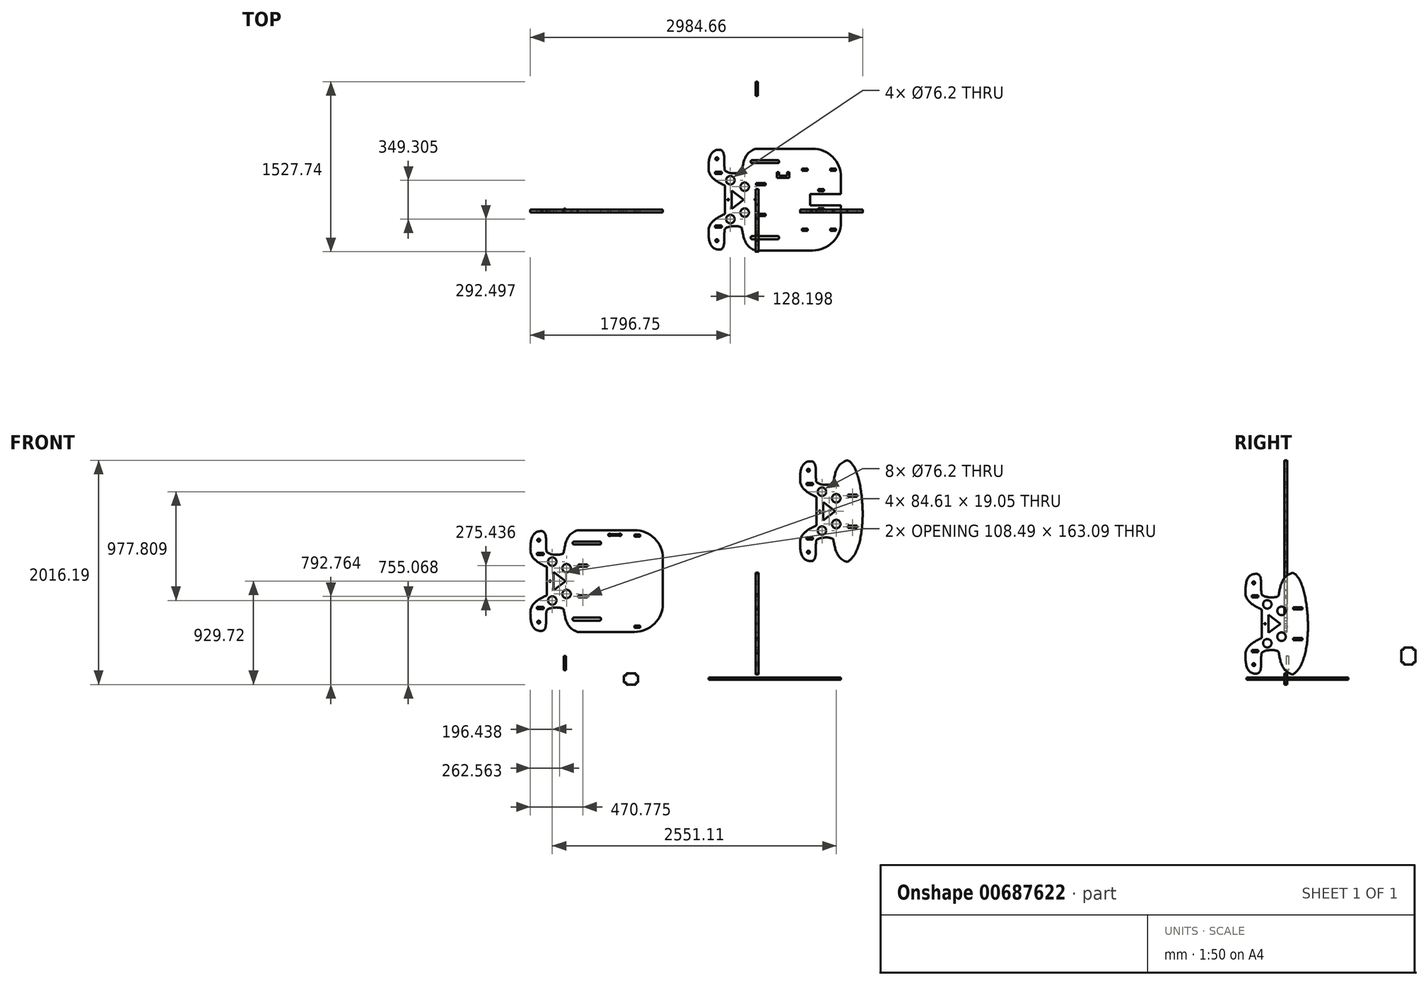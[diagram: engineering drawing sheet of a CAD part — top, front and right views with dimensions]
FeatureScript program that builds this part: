
annotation { "Feature Type Name" : "Feature", "Feature Type Description" : "" }
export const myFeature = defineFeature(function(context is Context, id is Id, definition is map)
    precondition{}
    {
        {
            var Q0;
            Q0=qCreatedBy(makeId("Top.planeOp"),FACE);
            var sketch = newSketch(context, id + "F0", { "sketchPlane" : qUnion([Q0])});
            skLineSegment(sketch, "E0.bottom", {"start": v(0, 548.5) * mm, "end": v(512.74, 548.5) * mm});
            skLineSegment(sketch, "E0.top", {"start": v(0, -365.9) * mm, "end": v(512.74, -365.9) * mm});
            skLineSegment(sketch, "E0.right", {"start": v(766.74, 294.5) * mm, "end": v(766.74, 142.1) * mm});
            skLineSegment(sketch, "E1", {"start": v(-107.03, 91.3) * mm, "end": v(491.23, 91.3) * mm});
            skLineSegment(sketch, "E2", {"start": v(461.94, 548.5) * mm, "end": v(461.94, -365.9) * mm, "construction": true});
            skPoint(sketch, "E3.visualSharp", {"position": v(766.74, -365.9) * mm});
            skArc(sketch, "E3.filletArc", {"start": v(512.74, -365.9) * mm, "mid": v(692.34, -291.51) * mm, "end": v(766.74, -111.9) * mm});
            skPoint(sketch, "E4.visualSharp", {"position": v(766.74, 548.5) * mm});
            skArc(sketch, "E4.filletArc", {"start": v(766.74, 294.5) * mm, "mid": v(692.34, 474.1) * mm, "end": v(512.74, 548.5) * mm});
            skLineSegment(sketch, "E5", {"start": v(210.85, -254.15) * mm, "end": v(210.85, -247.3) * mm});
            skLineSegment(sketch, "E6", {"start": v(200.7, -237.13) * mm, "end": v(-32.99, -237.13) * mm});
            skLineSegment(sketch, "E7", {"start": v(-43.15, -247.3) * mm, "end": v(-43.15, -254.15) * mm});
            skLineSegment(sketch, "E8", {"start": v(-32.99, -264.3) * mm, "end": v(200.7, -264.3) * mm});
            skPoint(sketch, "E9.visualSharp", {"position": v(-43.15, -237.13) * mm});
            skArc(sketch, "E9.filletArc", {"start": v(-32.99, -237.13) * mm, "mid": v(-40.17, -240.1) * mm, "end": v(-43.15, -247.3) * mm});
            skPoint(sketch, "E10.visualSharp", {"position": v(-43.15, -264.3) * mm});
            skArc(sketch, "E10.filletArc", {"start": v(-43.15, -254.15) * mm, "mid": v(-40.17, -261.33) * mm, "end": v(-32.99, -264.3) * mm});
            skPoint(sketch, "E11.visualSharp", {"position": v(210.85, -237.13) * mm});
            skArc(sketch, "E11.filletArc", {"start": v(210.85, -247.3) * mm, "mid": v(207.88, -240.1) * mm, "end": v(200.7, -237.13) * mm});
            skPoint(sketch, "E12.visualSharp", {"position": v(210.85, -264.3) * mm});
            skArc(sketch, "E12.filletArc", {"start": v(200.7, -264.3) * mm, "mid": v(207.88, -261.33) * mm, "end": v(210.85, -254.15) * mm});
            skLineSegment(sketch, "E13.MirrorCS", {"start": v(200.7, 419.71) * mm, "end": v(-32.99, 419.71) * mm});
            skArc(sketch, "E14.MirrorCS", {"start": v(210.85, 429.87) * mm, "mid": v(207.88, 422.69) * mm, "end": v(200.7, 419.71) * mm});
            skArc(sketch, "E15.MirrorCS", {"start": v(-32.99, 419.71) * mm, "mid": v(-40.17, 422.69) * mm, "end": v(-43.15, 429.87) * mm});
            skLineSegment(sketch, "E16.MirrorCS", {"start": v(210.85, 436.73) * mm, "end": v(210.85, 429.87) * mm});
            skLineSegment(sketch, "E17.MirrorCS", {"start": v(-43.15, 429.87) * mm, "end": v(-43.15, 436.73) * mm});
            skLineSegment(sketch, "E18", {"start": v(588.94, -354.2) * mm, "end": v(588.94, 40.5) * mm});
            skLineSegment(sketch, "E19", {"start": v(766.74, 294.5) * mm, "end": v(766.74, 142.1) * mm, "construction": true});
            skFitSpline(sketch, "E20.MirrorCS", {"points": [v(0, -365.9) * mm, v(-122.7, -173.52) * mm, v(-308.54, -21.5) * mm], "startDerivative": vector(-596.34, 198.24) * mm, "endDerivative": vector(-875.38, 6.78) * mm});
            skPoint(sketch, "E21", {"position": v(-43.15, -250.72) * mm});
            skLineSegment(sketch, "E22.MirrorCS", {"start": v(124.5, 91.3) * mm, "end": v(124.5, 90.53) * mm});
            skPoint(sketch, "E23.orphan", {"position": v(-15.2, 268.33) * mm});
            skLineSegment(sketch, "E24", {"start": v(-214.5, 172.07) * mm, "end": v(-214.5, 8.99) * mm});
            skCircle(sketch, "E25", {"center": v(-245.87, 90.53) * mm, "radius": 6.35 * mm});
            skCircle(sketch, "E26", {"center": v(-98.19, -25.5) * mm, "radius": 38.1 * mm});
            skPoint(sketch, "E27.positionSnap0", {"position": v(-320.15, -344.34) * mm});
            skPoint(sketch, "E28.MirrorP", {"position": v(-43.15, 431.78) * mm});
            skPoint(sketch, "E29.MirrorP", {"position": v(-43.15, 445.37) * mm});
            skPoint(sketch, "E30.MirrorP", {"position": v(-43.15, 418.19) * mm});
            skLineSegment(sketch, "E31", {"start": v(-214.5, 8.99) * mm, "end": v(-106.02, 90.53) * mm});
            skLineSegment(sketch, "E32.MirrorCS", {"start": v(-214.5, 172.07) * mm, "end": v(-106.02, 90.53) * mm});
            skCircle(sketch, "E33.MirrorC", {"center": v(-226.39, -84.12) * mm, "radius": 38.1 * mm});
            skCircle(sketch, "E34.MirrorC", {"center": v(-347.9, -277.34) * mm, "radius": 12.7 * mm});
            skPoint(sketch, "E35.MirrorP", {"position": v(-324.04, -277.34) * mm});
            skFitSpline(sketch, "E36.MirrorCS", {"points": [v(-320.15, -358.3) * mm, v(-277.34, -173.78) * mm], "startDerivative": vector(168, 45.32) * mm, "endDerivative": vector(42.54, 297.2) * mm});
            skFitSpline(sketch, "E37.MirrorCS", {"points": [v(-320.15, -358.3) * mm, v(-407.1, -21.15) * mm], "startDerivative": vector(-410.48, -21.33) * mm, "endDerivative": vector(48.12, 416.26) * mm});
            skFitSpline(sketch, "E38", {"points": [v(-123.95, -167.42) * mm, v(-277.34, -173.78) * mm], "startDerivative": vector(-0.87, 82.52) * mm, "endDerivative": vector(-81, -110.74) * mm});
            skFitSpline(sketch, "E39", {"points": [v(-276.57, -37.66) * mm, v(-422.21, -174.57) * mm], "startDerivative": vector(-229.66, -105.01) * mm, "endDerivative": vector(-27.76, -191.38) * mm});
            skFitSpline(sketch, "E40.MirrorCS", {"points": [v(0, 548.5) * mm, v(-122.7, 356.1) * mm, v(-308.54, 204.08) * mm], "startDerivative": vector(-596.34, -198.24) * mm, "endDerivative": vector(-875.38, -6.78) * mm});
            skLineSegment(sketch, "E41.MirrorCS", {"start": v(-43.15, 428.35) * mm, "end": v(-43.15, 435.2) * mm});
            skArc(sketch, "E42.MirrorCS", {"start": v(200.7, 445.37) * mm, "mid": v(207.88, 442.4) * mm, "end": v(210.85, 435.2) * mm});
            skLineSegment(sketch, "E43.MirrorCS", {"start": v(210.85, 435.2) * mm, "end": v(210.85, 428.35) * mm});
            skArc(sketch, "E44.MirrorCS", {"start": v(-43.15, 435.2) * mm, "mid": v(-40.17, 442.4) * mm, "end": v(-32.99, 445.37) * mm});
            skCircle(sketch, "E45.MirrorC", {"center": v(-347.9, 458.4) * mm, "radius": 12.7 * mm});
            skFitSpline(sketch, "E46.MirrorCS", {"points": [v(-320.15, 539.35) * mm, v(-407.1, 202.21) * mm], "startDerivative": vector(-410.48, 21.33) * mm, "endDerivative": vector(48.12, -416.26) * mm});
            skFitSpline(sketch, "E47.MirrorCS", {"points": [v(-276.57, 218.72) * mm, v(-422.21, 355.63) * mm], "startDerivative": vector(-229.66, 105.01) * mm, "endDerivative": vector(-27.76, 191.38) * mm});
            skCircle(sketch, "E48.MirrorC", {"center": v(-98.19, 206.56) * mm, "radius": 38.1 * mm});
            skPoint(sketch, "E49.MirrorP", {"position": v(-324.04, 458.4) * mm});
            skFitSpline(sketch, "E50.MirrorCS", {"points": [v(-123.95, 348.48) * mm, v(-277.34, 354.84) * mm], "startDerivative": vector(-0.87, -82.52) * mm, "endDerivative": vector(-81, 110.74) * mm});
            skLineSegment(sketch, "E51.MirrorCS", {"start": v(-32.99, 445.37) * mm, "end": v(200.7, 445.37) * mm});
            skCircle(sketch, "E52.MirrorC", {"center": v(-226.39, 265.18) * mm, "radius": 38.1 * mm});
            skPoint(sketch, "E53.MirrorP", {"position": v(210.85, 418.19) * mm});
            skPoint(sketch, "E54.MirrorP", {"position": v(-320.15, 525.4) * mm});
            skFitSpline(sketch, "E55.MirrorCS", {"points": [v(-320.15, 539.35) * mm, v(-277.34, 354.84) * mm], "startDerivative": vector(168, -45.32) * mm, "endDerivative": vector(42.54, -297.2) * mm});
            skPoint(sketch, "E56.MirrorP", {"position": v(210.85, 445.37) * mm});
            skPoint(sketch, "E57.MirrorP", {"position": v(0, 546.97) * mm});
            skLineSegment(sketch, "E58", {"start": v(-276.57, -37.66) * mm, "end": v(-276.57, 218.72) * mm});
            skFitSpline(sketch, "E59", {"points": [v(-123.95, 348.48) * mm, v(-123.95, 350) * mm], "startDerivative": vector(0.09, 0.95) * mm, "endDerivative": vector(0.33, 1.62) * mm});
            skLineSegment(sketch, "E60.MirrorCS", {"start": v(5.64, 219.48) * mm, "end": v(90.26, 219.48) * mm});
            skLineSegment(sketch, "E61.MirrorCS", {"start": v(5.64, 238.53) * mm, "end": v(5.64, 219.48) * mm});
            skLineSegment(sketch, "E62.MirrorCS", {"start": v(90.26, 238.53) * mm, "end": v(90.26, 219.48) * mm});
            skLineSegment(sketch, "E63.MirrorCS", {"start": v(5.64, 238.53) * mm, "end": v(90.26, 238.53) * mm});
            skLineSegment(sketch, "E64.MirrorCS", {"start": v(5.64, -36.9) * mm, "end": v(90.26, -36.9) * mm});
            skLineSegment(sketch, "E65.MirrorCS", {"start": v(5.64, -55.95) * mm, "end": v(90.26, -55.95) * mm});
            skLineSegment(sketch, "E66.MirrorCS", {"start": v(5.64, -55.95) * mm, "end": v(5.64, -36.9) * mm});
            skLineSegment(sketch, "E67.MirrorCS", {"start": v(90.26, -55.95) * mm, "end": v(90.26, -36.9) * mm});
            skLineSegment(sketch, "E68.bottom", {"start": v(-362.9, 342.54) * mm, "end": v(-305.3, 342.54) * mm});
            skLineSegment(sketch, "E68.top", {"start": v(-362.9, 323.49) * mm, "end": v(-305.3, 323.49) * mm});
            skLineSegment(sketch, "E68.left", {"start": v(-362.9, 342.54) * mm, "end": v(-362.9, 323.49) * mm});
            skLineSegment(sketch, "E68.right", {"start": v(-305.3, 342.54) * mm, "end": v(-305.3, 323.49) * mm});
            skLineSegment(sketch, "E69", {"start": v(-106.02, 90.53) * mm, "end": v(-545.67, 90.53) * mm});
            skLineSegment(sketch, "E70.MirrorCS", {"start": v(-362.9, -161.48) * mm, "end": v(-305.3, -161.48) * mm});
            skLineSegment(sketch, "E71.MirrorCS", {"start": v(-362.9, -142.43) * mm, "end": v(-305.3, -142.43) * mm});
            skLineSegment(sketch, "E72.MirrorCS", {"start": v(-362.9, -161.48) * mm, "end": v(-362.9, -142.43) * mm});
            skLineSegment(sketch, "E73.MirrorCS", {"start": v(-305.3, -161.48) * mm, "end": v(-305.3, -142.43) * mm});
            skLineSegment(sketch, "E74", {"start": v(-422.21, 355.63) * mm, "end": v(-277.34, 354.84) * mm, "construction": true});
            skPoint(sketch, "E75.endSnap0", {"position": v(210.85, 433.3) * mm});
            skPoint(sketch, "E76", {"position": v(461.94, 370.7) * mm});
            skPoint(sketch, "E77", {"position": v(461.94, -188.1) * mm});
            skLineSegment(sketch, "E78", {"start": v(755.04, 370.7) * mm, "end": v(223.96, 370.7) * mm, "construction": true});
            skLineSegment(sketch, "E79.bottom", {"start": v(418.05, 370.7) * mm, "end": v(468.85, 370.7) * mm});
            skLineSegment(sketch, "E79.top", {"start": v(418.05, 351.64) * mm, "end": v(468.85, 351.64) * mm});
            skLineSegment(sketch, "E79.left", {"start": v(418.05, 370.7) * mm, "end": v(418.05, 351.64) * mm});
            skLineSegment(sketch, "E79.right", {"start": v(468.85, 370.7) * mm, "end": v(468.85, 351.64) * mm});
            skLineSegment(sketch, "E80.bottom", {"start": v(672.05, 370.7) * mm, "end": v(722.85, 370.7) * mm});
            skLineSegment(sketch, "E80.top", {"start": v(672.05, 351.64) * mm, "end": v(722.85, 351.64) * mm});
            skLineSegment(sketch, "E80.left", {"start": v(672.05, 370.7) * mm, "end": v(672.05, 351.64) * mm});
            skLineSegment(sketch, "E80.right", {"start": v(722.85, 370.7) * mm, "end": v(722.85, 351.64) * mm});
            skLineSegment(sketch, "E81.MirrorCS", {"start": v(418.05, -188.1) * mm, "end": v(468.85, -188.1) * mm});
            skLineSegment(sketch, "E82.MirrorCS", {"start": v(418.05, -188.1) * mm, "end": v(418.05, -169.06) * mm});
            skLineSegment(sketch, "E83.MirrorCS", {"start": v(418.05, -169.06) * mm, "end": v(468.85, -169.06) * mm});
            skLineSegment(sketch, "E84.MirrorCS", {"start": v(468.85, -188.1) * mm, "end": v(468.85, -169.06) * mm});
            skLineSegment(sketch, "E85.MirrorCS", {"start": v(672.05, -188.1) * mm, "end": v(722.85, -188.1) * mm});
            skLineSegment(sketch, "E86.MirrorCS", {"start": v(672.05, -188.1) * mm, "end": v(672.05, -169.06) * mm});
            skLineSegment(sketch, "E87.MirrorCS", {"start": v(672.05, -169.06) * mm, "end": v(722.85, -169.06) * mm});
            skLineSegment(sketch, "E88.MirrorCS", {"start": v(722.85, -188.1) * mm, "end": v(722.85, -169.06) * mm});
            skPoint(sketch, "E89", {"position": v(461.94, 91.3) * mm});
            skPoint(sketch, "E90", {"position": v(461.94, 40.5) * mm});
            skPoint(sketch, "E91", {"position": v(461.94, 142.1) * mm});
            skLineSegment(sketch, "E92.left", {"start": v(491.23, 40.5) * mm, "end": v(491.23, 142.1) * mm});
            skLineSegment(sketch, "E93.bottom", {"start": v(563.54, 167.5) * mm, "end": v(614.34, 167.5) * mm});
            skLineSegment(sketch, "E93.top", {"start": v(563.54, 186.54) * mm, "end": v(614.34, 186.54) * mm});
            skLineSegment(sketch, "E93.left", {"start": v(563.54, 167.5) * mm, "end": v(563.54, 186.54) * mm});
            skLineSegment(sketch, "E93.right", {"start": v(614.34, 167.5) * mm, "end": v(614.34, 186.54) * mm});
            skLineSegment(sketch, "E94.MirrorCS", {"start": v(563.54, 15.1) * mm, "end": v(614.34, 15.1) * mm});
            skLineSegment(sketch, "E95.MirrorCS", {"start": v(563.54, -3.96) * mm, "end": v(614.34, -3.96) * mm});
            skLineSegment(sketch, "E96.MirrorCS", {"start": v(563.54, 15.1) * mm, "end": v(563.54, -3.96) * mm});
            skLineSegment(sketch, "E97.MirrorCS", {"start": v(614.34, 15.1) * mm, "end": v(614.34, -3.96) * mm});
            skCircle(sketch, "E98", {"center": v(0, 91.3) * mm, "radius": 8.9 * mm});
            skPoint(sketch, "E98.centerSnap0", {"position": v(697.45, -169.06) * mm});
            skLineSegment(sketch, "E99", {"start": v(491.23, 142.1) * mm, "end": v(766.74, 142.1) * mm});
            skLineSegment(sketch, "E100", {"start": v(491.23, 40.5) * mm, "end": v(766.74, 40.5) * mm});
            skLineSegment(sketch, "E101.trimOffspring", {"start": v(766.74, 40.5) * mm, "end": v(766.74, -111.9) * mm, "construction": true});
            skLineSegment(sketch, "E102.trimOffspring", {"start": v(766.74, 40.5) * mm, "end": v(766.74, -111.9) * mm});
            skPoint(sketch, "E103.orphan", {"position": v(766.74, 91.3) * mm});
            skLineSegment(sketch, "E104.trimOffspring", {"start": v(588.94, 142.1) * mm, "end": v(588.94, 536.8) * mm});
            skLineSegment(sketch, "E105", {"start": v(246.34, 305.67) * mm, "end": v(281.83, 305.67) * mm});
            skLineSegment(sketch, "E106", {"start": v(281.83, 305.67) * mm, "end": v(281.83, 337.71) * mm});
            skLineSegment(sketch, "E107", {"start": v(281.83, 337.71) * mm, "end": v(300.88, 337.71) * mm});
            skLineSegment(sketch, "E108", {"start": v(300.88, 337.71) * mm, "end": v(300.88, 286.62) * mm});
            skLineSegment(sketch, "E109", {"start": v(300.88, 286.62) * mm, "end": v(246.34, 286.62) * mm});
            skPoint(sketch, "E110.startSnap0", {"position": v(246.34, 305.67) * mm});
            skPoint(sketch, "E111.end.orphan", {"position": v(210.85, 338.7) * mm});
            skPoint(sketch, "E112.orphan", {"position": v(210.85, 305.67) * mm});
            skLineSegment(sketch, "E113.MirrorCS", {"start": v(191.8, 337.71) * mm, "end": v(191.8, 286.62) * mm});
            skLineSegment(sketch, "E114.MirrorCS", {"start": v(210.85, 337.71) * mm, "end": v(191.8, 337.71) * mm});
            skLineSegment(sketch, "E115.MirrorCS", {"start": v(210.85, 305.67) * mm, "end": v(210.85, 337.71) * mm});
            skLineSegment(sketch, "E116.MirrorCS", {"start": v(246.34, 305.67) * mm, "end": v(210.85, 305.67) * mm});
            skLineSegment(sketch, "E117.MirrorCS", {"start": v(191.8, 286.62) * mm, "end": v(246.34, 286.62) * mm});
            skPoint(sketch, "E118.orphan", {"position": v(246.34, 360) * mm});
            skSolve(sketch);
        }
        {
            var Q0;
            Q0=qCreatedBy(makeId("Front.planeOp"),FACE);
            var sketch = newSketch(context, id + "F1", { "sketchPlane" : qUnion([Q0])});
            skLineSegment(sketch, "E119.bottom", {"start": v(-1714.56, 86.36) * mm, "end": v(-1724.72, 86.36) * mm});
            skLineSegment(sketch, "E119.top", {"start": v(-1714.56, 213.36) * mm, "end": v(-1724.72, 213.36) * mm});
            skLineSegment(sketch, "E119.left", {"start": v(-1714.56, 86.36) * mm, "end": v(-1714.56, 213.36) * mm});
            skLineSegment(sketch, "E119.right", {"start": v(-1724.72, 86.36) * mm, "end": v(-1724.72, 213.36) * mm});
            skPoint(sketch, "E119.middle", {"position": v(-1719.64, 149.86) * mm});
            skSolve(sketch);
        }
        {
            var Q0;
            Q0=makeQuery(id+"F1.imprint","IMPRINT",FACE,{"disambiguationData":[TD([[makeQuery(id+"F1.imprint","IMPRINT",EDGE,{"derivedFrom":sQuery(id+"F1.wireOp",EDGE,"E119.bottom")}),-1.0]])]});
            var Q1;
            Q1=sQuery(id+"F1.wireOp",EDGE,"E119.left");
            revolve(context, id + "F2", {"entities" : qUnion([Q0]), "axis" : qUnion([Q1]), "revolveType" : RevolveType.FULL});
        }
        {
            var Q0;
            Q0=qSketchRegion(id+"F0",true);
            extrude(context, id + "F3", {"entities" : qUnion([Q0]), "depth" : 19.05 * mm, "offsetDistance" : 25.4 * mm});
        }
        {
            var Q0;
            Q0=qCreatedBy(makeId("Right.planeOp"),FACE);
            var sketch = newSketch(context, id + "F4", { "sketchPlane" : qUnion([Q0])});
            skFitSpline(sketch, "E120.MirrorCS", {"points": [v(46.21, 47.06) * mm, v(-76.5, 239.45) * mm, v(-262.33, 391.47) * mm], "startDerivative": vector(-596.34, 198.24) * mm, "endDerivative": vector(-875.38, 6.78) * mm});
            skLineSegment(sketch, "E121", {"start": v(-168.3, 585.05) * mm, "end": v(-168.3, 421.96) * mm});
            skCircle(sketch, "E122", {"center": v(-199.66, 503.5) * mm, "radius": 6.35 * mm});
            skCircle(sketch, "E123", {"center": v(-51.98, 387.47) * mm, "radius": 38.1 * mm});
            skPoint(sketch, "E124.positionSnap0", {"position": v(-273.94, 68.63) * mm});
            skLineSegment(sketch, "E125", {"start": v(-168.3, 421.96) * mm, "end": v(-59.8, 503.5) * mm});
            skLineSegment(sketch, "E126.MirrorCS", {"start": v(-168.3, 585.05) * mm, "end": v(-59.8, 503.5) * mm});
            skCircle(sketch, "E127.MirrorC", {"center": v(-180.17, 328.85) * mm, "radius": 38.1 * mm});
            skCircle(sketch, "E128.MirrorC", {"center": v(-301.7, 135.64) * mm, "radius": 12.7 * mm});
            skPoint(sketch, "E129.MirrorP", {"position": v(-277.83, 135.64) * mm});
            skFitSpline(sketch, "E130.MirrorCS", {"points": [v(-273.94, 54.68) * mm, v(-231.14, 240.68) * mm], "startDerivative": vector(168, 45.32) * mm, "endDerivative": vector(42.54, 297.2) * mm});
            skFitSpline(sketch, "E131.MirrorCS", {"points": [v(-273.94, 54.68) * mm, v(-360.89, 391.82) * mm], "startDerivative": vector(-410.48, -21.33) * mm, "endDerivative": vector(48.12, 416.26) * mm});
            skFitSpline(sketch, "E132", {"points": [v(-77.74, 245.55) * mm, v(-231.14, 240.68) * mm], "startDerivative": vector(-0.87, 82.52) * mm, "endDerivative": vector(-81, -110.74) * mm});
            skFitSpline(sketch, "E133", {"points": [v(-230.36, 375.3) * mm, v(-376, 238.4) * mm], "startDerivative": vector(-229.66, -105.01) * mm, "endDerivative": vector(-27.76, -191.38) * mm});
            skFitSpline(sketch, "E134.MirrorCS", {"points": [v(46.21, 961.46) * mm, v(-76.5, 769.07) * mm, v(-262.33, 617.06) * mm], "startDerivative": vector(-596.34, -198.24) * mm, "endDerivative": vector(-875.38, -6.78) * mm});
            skCircle(sketch, "E135.MirrorC", {"center": v(-301.7, 871.37) * mm, "radius": 12.7 * mm});
            skFitSpline(sketch, "E136.MirrorCS", {"points": [v(-273.94, 952.33) * mm, v(-360.89, 615.19) * mm], "startDerivative": vector(-410.48, 21.33) * mm, "endDerivative": vector(48.12, -416.26) * mm});
            skFitSpline(sketch, "E137.MirrorCS", {"points": [v(-230.36, 631.7) * mm, v(-376, 768.6) * mm], "startDerivative": vector(-229.66, 105.01) * mm, "endDerivative": vector(-27.76, 191.38) * mm});
            skCircle(sketch, "E138.MirrorC", {"center": v(-51.98, 619.54) * mm, "radius": 38.1 * mm});
            skPoint(sketch, "E139.MirrorP", {"position": v(-277.83, 871.37) * mm});
            skFitSpline(sketch, "E140.MirrorCS", {"points": [v(-77.74, 761.46) * mm, v(-231.13, 767.8) * mm], "startDerivative": vector(-0.87, -82.52) * mm, "endDerivative": vector(-81, 110.74) * mm});
            skCircle(sketch, "E141.MirrorC", {"center": v(-180.17, 678.15) * mm, "radius": 38.1 * mm});
            skPoint(sketch, "E142.MirrorP", {"position": v(-273.94, 938.38) * mm});
            skFitSpline(sketch, "E143.MirrorCS", {"points": [v(-273.94, 952.33) * mm, v(-231.13, 767.8) * mm], "startDerivative": vector(168, -45.32) * mm, "endDerivative": vector(42.54, -297.2) * mm});
            skLineSegment(sketch, "E144", {"start": v(-230.36, 375.3) * mm, "end": v(-230.36, 631.7) * mm});
            skFitSpline(sketch, "E145", {"points": [v(-77.74, 761.46) * mm, v(-77.74, 762.98) * mm], "startDerivative": vector(0.09, 0.95) * mm, "endDerivative": vector(0.33, 1.62) * mm});
            skFitSpline(sketch, "E146", {"points": [v(46.21, 961.46) * mm, v(46.21, 47.06) * mm], "startDerivative": vector(461.05, -112.6) * mm, "endDerivative": vector(-642.98, -332.06) * mm});
            skLineSegment(sketch, "E147.bottom", {"start": v(51.86, 632.46) * mm, "end": v(136.47, 632.46) * mm});
            skLineSegment(sketch, "E147.top", {"start": v(51.86, 651.5) * mm, "end": v(136.47, 651.5) * mm});
            skLineSegment(sketch, "E147.left", {"start": v(51.86, 632.46) * mm, "end": v(51.86, 651.5) * mm});
            skLineSegment(sketch, "E147.right", {"start": v(136.47, 632.46) * mm, "end": v(136.47, 651.5) * mm});
            skLineSegment(sketch, "E148", {"start": v(-59.8, 503.5) * mm, "end": v(281.17, 503.5) * mm});
            skLineSegment(sketch, "E149", {"start": v(141.4, 175.84) * mm, "end": v(13.23, 175.84) * mm});
            skLineSegment(sketch, "E150", {"start": v(3.07, 165.68) * mm, "end": v(3.07, 158.82) * mm});
            skLineSegment(sketch, "E151", {"start": v(13.23, 148.66) * mm, "end": v(130.44, 148.66) * mm});
            skPoint(sketch, "E152.visualSharp", {"position": v(3.07, 175.84) * mm});
            skArc(sketch, "E152.filletArc", {"start": v(13.23, 175.84) * mm, "mid": v(6.04, 172.87) * mm, "end": v(3.07, 165.68) * mm});
            skPoint(sketch, "E153.visualSharp", {"position": v(3.07, 148.66) * mm});
            skArc(sketch, "E153.filletArc", {"start": v(3.07, 158.82) * mm, "mid": v(6.04, 151.64) * mm, "end": v(13.23, 148.66) * mm});
            skFitSpline(sketch, "E154.MirrorCS", {"points": [v(46.21, 47.06) * mm, v(-76.5, 239.45) * mm, v(-262.33, 391.47) * mm], "startDerivative": vector(-596.34, 198.24) * mm, "endDerivative": vector(-875.38, 6.78) * mm});
            skPoint(sketch, "E155", {"position": v(3.07, 162.25) * mm});
            skArc(sketch, "E156.MirrorCS", {"start": v(13.23, 831.16) * mm, "mid": v(6.04, 834.14) * mm, "end": v(3.07, 841.32) * mm});
            skArc(sketch, "E157.MirrorCS", {"start": v(3.07, 848.18) * mm, "mid": v(6.04, 855.36) * mm, "end": v(13.23, 858.34) * mm});
            skLineSegment(sketch, "E158.MirrorCS", {"start": v(3.07, 841.32) * mm, "end": v(3.07, 848.18) * mm});
            skLineSegment(sketch, "E159.MirrorCS", {"start": v(137.14, 831.16) * mm, "end": v(13.23, 831.16) * mm});
            skPoint(sketch, "E160.MirrorP", {"position": v(3.07, 858.34) * mm});
            skPoint(sketch, "E161.MirrorP", {"position": v(3.07, 831.16) * mm});
            skPoint(sketch, "E162.MirrorP", {"position": v(3.07, 844.75) * mm});
            skLineSegment(sketch, "E163.MirrorCS", {"start": v(13.23, 858.34) * mm, "end": v(127.47, 858.34) * mm});
            skLineSegment(sketch, "E164.MirrorCS", {"start": v(51.86, 355.5) * mm, "end": v(136.47, 355.5) * mm});
            skLineSegment(sketch, "E165.MirrorCS", {"start": v(51.86, 374.55) * mm, "end": v(136.47, 374.55) * mm});
            skLineSegment(sketch, "E166.MirrorCS", {"start": v(51.86, 374.55) * mm, "end": v(51.86, 355.5) * mm});
            skLineSegment(sketch, "E167.MirrorCS", {"start": v(136.47, 374.55) * mm, "end": v(136.47, 355.5) * mm});
            skLineSegment(sketch, "E168", {"start": v(-231.14, 240.68) * mm, "end": v(-376, 238.4) * mm, "construction": true});
            skLineSegment(sketch, "E169.bottom", {"start": v(-260.66, 267.57) * mm, "end": v(-318.26, 267.57) * mm});
            skLineSegment(sketch, "E169.top", {"start": v(-260.66, 248.52) * mm, "end": v(-318.26, 248.52) * mm});
            skLineSegment(sketch, "E169.left", {"start": v(-260.66, 267.57) * mm, "end": v(-260.66, 248.52) * mm});
            skLineSegment(sketch, "E169.right", {"start": v(-318.26, 267.57) * mm, "end": v(-318.26, 248.52) * mm});
            skLineSegment(sketch, "E170.MirrorCS", {"start": v(-260.66, 739.44) * mm, "end": v(-318.26, 739.44) * mm});
            skLineSegment(sketch, "E171.MirrorCS", {"start": v(-260.66, 758.49) * mm, "end": v(-318.26, 758.49) * mm});
            skLineSegment(sketch, "E172.MirrorCS", {"start": v(-318.26, 739.44) * mm, "end": v(-318.26, 758.49) * mm});
            skLineSegment(sketch, "E173.MirrorCS", {"start": v(-260.66, 739.44) * mm, "end": v(-260.66, 758.49) * mm});
            skSolve(sketch);
        }
        {
            var Q0;
            Q0=qSketchRegion(id+"F4",true);
            extrude(context, id + "F5", {"entities" : qUnion([Q0]), "depth" : 25.4 * mm, "offsetDistance" : 25.4 * mm});
        }
        {
            var Q0;
            Q0=qCreatedBy(makeId("Right.planeOp"),FACE);
            var sketch = newSketch(context, id + "F6", { "sketchPlane" : qUnion([Q0])});
            skLineSegment(sketch, "E174.bottom", {"start": v(1024.12, 270.76) * mm, "end": v(1151.12, 270.76) * mm});
            skLineSegment(sketch, "E174.top", {"start": v(1024.12, 156.46) * mm, "end": v(1151.12, 156.46) * mm});
            skLineSegment(sketch, "E174.left", {"start": v(1024.12, 270.76) * mm, "end": v(1024.12, 156.46) * mm});
            skLineSegment(sketch, "E174.right", {"start": v(1151.12, 270.76) * mm, "end": v(1151.12, 156.46) * mm});
            skLineSegment(sketch, "E175", {"start": v(1087.62, 270.76) * mm, "end": v(1087.62, 156.46) * mm, "construction": true});
            skLineSegment(sketch, "E176", {"start": v(1045.31, 270.76) * mm, "end": v(1045.31, 289.8) * mm});
            skLineSegment(sketch, "E177", {"start": v(1045.31, 289.8) * mm, "end": v(1129.93, 289.8) * mm});
            skLineSegment(sketch, "E178", {"start": v(1129.93, 289.8) * mm, "end": v(1129.93, 270.76) * mm});
            skLineSegment(sketch, "E179", {"start": v(1024.12, 213.6) * mm, "end": v(1151.12, 213.6) * mm, "construction": true});
            skLineSegment(sketch, "E180.MirrorCS", {"start": v(1045.31, 156.46) * mm, "end": v(1045.31, 137.4) * mm});
            skLineSegment(sketch, "E181.MirrorCS", {"start": v(1045.31, 137.4) * mm, "end": v(1129.93, 137.4) * mm});
            skLineSegment(sketch, "E182.MirrorCS", {"start": v(1129.93, 137.4) * mm, "end": v(1129.93, 156.46) * mm});
            skSolve(sketch);
        }
        {
            var Q0;
            {var subQ0=sQuery(id+"F6.wireOp",EDGE,"E174.left");Q0=makeQuery(id+"F6.imprint","IMPRINT",FACE,{"disambiguationData":[TD([[makeQuery(id+"F6.imprint","IMPRINT",EDGE,{"derivedFrom":subQ0}),1.0]])]});}
            var Q1;
            {var subQ0=sQuery(id+"F6.wireOp",EDGE,"E176");Q1=makeQuery(id+"F6.imprint","IMPRINT",FACE,{"disambiguationData":[TD([[makeQuery(id+"F6.imprint","IMPRINT",EDGE,{"derivedFrom":subQ0}),-1.0]])]});}
            var Q2;
            {var subQ0=sQuery(id+"F6.wireOp",EDGE,"E180.MirrorCS");Q2=makeQuery(id+"F6.imprint","IMPRINT",FACE,{"disambiguationData":[TD([[makeQuery(id+"F6.imprint","IMPRINT",EDGE,{"derivedFrom":subQ0}),1.0]])]});}
            extrude(context, id + "F7", {"entities" : qUnion([Q0, Q1, Q2]), "depth" : 19.05 * mm, "offsetDistance" : 25.4 * mm});
        }
        {
            var Q0;
            Q0=qCreatedBy(makeId("Front.planeOp"),FACE);
            var sketch = newSketch(context, id + "F8", { "sketchPlane" : qUnion([Q0])});
            skLineSegment(sketch, "E183.bottom", {"start": v(-1182.42, 39.8) * mm, "end": v(-1055.42, 39.8) * mm});
            skLineSegment(sketch, "E183.top", {"start": v(-1182.42, -23.7) * mm, "end": v(-1055.42, -23.7) * mm});
            skLineSegment(sketch, "E183.left", {"start": v(-1182.42, 39.8) * mm, "end": v(-1182.42, -23.7) * mm});
            skLineSegment(sketch, "E183.right", {"start": v(-1055.42, 39.8) * mm, "end": v(-1055.42, -23.7) * mm});
            skLineSegment(sketch, "E184", {"start": v(-1118.92, 39.8) * mm, "end": v(-1118.92, -23.7) * mm, "construction": true});
            skLineSegment(sketch, "E185", {"start": v(-1161.23, 39.8) * mm, "end": v(-1161.23, 58.85) * mm});
            skLineSegment(sketch, "E186", {"start": v(-1161.23, 58.85) * mm, "end": v(-1076.62, 58.85) * mm});
            skLineSegment(sketch, "E187", {"start": v(-1076.62, 58.85) * mm, "end": v(-1076.62, 39.8) * mm});
            skLineSegment(sketch, "E188", {"start": v(-1182.42, 8.05) * mm, "end": v(-1055.42, 8.05) * mm, "construction": true});
            skLineSegment(sketch, "E189.MirrorCS", {"start": v(-1161.23, -23.7) * mm, "end": v(-1161.23, -42.75) * mm});
            skLineSegment(sketch, "E190.MirrorCS", {"start": v(-1161.23, -42.75) * mm, "end": v(-1076.62, -42.75) * mm});
            skLineSegment(sketch, "E191.MirrorCS", {"start": v(-1076.62, -42.75) * mm, "end": v(-1076.62, -23.7) * mm});
            skLineSegment(sketch, "E192.bottom", {"start": v(-1600.32, 1344.93) * mm, "end": v(-1087.58, 1344.93) * mm});
            skLineSegment(sketch, "E192.top", {"start": v(-1600.32, 430.53) * mm, "end": v(-1087.58, 430.53) * mm});
            skLineSegment(sketch, "E192.right", {"start": v(-833.58, 1090.93) * mm, "end": v(-833.58, 684.53) * mm});
            skLineSegment(sketch, "E193", {"start": v(-1707.35, 887.73) * mm, "end": v(-833.58, 887.73) * mm});
            skLineSegment(sketch, "E194", {"start": v(-1138.38, 1344.93) * mm, "end": v(-1138.38, 430.53) * mm, "construction": true});
            skPoint(sketch, "E195.visualSharp", {"position": v(-833.58, 430.53) * mm});
            skArc(sketch, "E195.filletArc", {"start": v(-1087.58, 430.53) * mm, "mid": v(-907.97, 504.93) * mm, "end": v(-833.58, 684.53) * mm});
            skPoint(sketch, "E196.visualSharp", {"position": v(-833.58, 1344.93) * mm});
            skArc(sketch, "E196.filletArc", {"start": v(-833.58, 1090.93) * mm, "mid": v(-907.97, 1270.54) * mm, "end": v(-1087.58, 1344.93) * mm});
            skLineSegment(sketch, "E197", {"start": v(-1389.46, 542.3) * mm, "end": v(-1389.46, 549.15) * mm});
            skLineSegment(sketch, "E198", {"start": v(-1399.62, 559.31) * mm, "end": v(-1633.3, 559.31) * mm});
            skLineSegment(sketch, "E199", {"start": v(-1643.46, 549.15) * mm, "end": v(-1643.46, 542.3) * mm});
            skLineSegment(sketch, "E200", {"start": v(-1633.3, 532.13) * mm, "end": v(-1399.62, 532.13) * mm});
            skPoint(sketch, "E201.visualSharp", {"position": v(-1643.46, 559.31) * mm});
            skArc(sketch, "E201.filletArc", {"start": v(-1633.3, 559.31) * mm, "mid": v(-1640.49, 556.33) * mm, "end": v(-1643.46, 549.15) * mm});
            skPoint(sketch, "E202.visualSharp", {"position": v(-1643.46, 532.13) * mm});
            skArc(sketch, "E202.filletArc", {"start": v(-1643.46, 542.3) * mm, "mid": v(-1640.49, 535.1) * mm, "end": v(-1633.3, 532.13) * mm});
            skPoint(sketch, "E203.visualSharp", {"position": v(-1389.46, 559.31) * mm});
            skArc(sketch, "E203.filletArc", {"start": v(-1389.46, 549.15) * mm, "mid": v(-1392.44, 556.33) * mm, "end": v(-1399.62, 559.31) * mm});
            skPoint(sketch, "E204.visualSharp", {"position": v(-1389.46, 532.13) * mm});
            skArc(sketch, "E204.filletArc", {"start": v(-1399.62, 532.13) * mm, "mid": v(-1392.44, 535.1) * mm, "end": v(-1389.46, 542.3) * mm});
            skLineSegment(sketch, "E205.MirrorCS", {"start": v(-1399.62, 1216.15) * mm, "end": v(-1633.3, 1216.15) * mm});
            skArc(sketch, "E206.MirrorCS", {"start": v(-1389.46, 1226.31) * mm, "mid": v(-1392.44, 1219.13) * mm, "end": v(-1399.62, 1216.15) * mm});
            skArc(sketch, "E207.MirrorCS", {"start": v(-1633.3, 1216.15) * mm, "mid": v(-1640.49, 1219.13) * mm, "end": v(-1643.46, 1226.31) * mm});
            skLineSegment(sketch, "E208.MirrorCS", {"start": v(-1389.46, 1233.17) * mm, "end": v(-1389.46, 1226.31) * mm});
            skLineSegment(sketch, "E209.MirrorCS", {"start": v(-1643.46, 1226.31) * mm, "end": v(-1643.46, 1233.17) * mm});
            skLineSegment(sketch, "E210", {"start": v(-1011.38, 442.23) * mm, "end": v(-1011.38, 1333.23) * mm});
            skLineSegment(sketch, "E211", {"start": v(-833.58, 1090.93) * mm, "end": v(-833.58, 684.53) * mm, "construction": true});
            skLineSegment(sketch, "E212", {"start": v(-1302.28, 1309.01) * mm, "end": v(-1226.08, 1309.01) * mm});
            skLineSegment(sketch, "E213", {"start": v(-1302.28, 1297.32) * mm, "end": v(-1226.08, 1297.32) * mm});
            skArc(sketch, "E214", {"start": v(-1226.08, 1297.67) * mm, "mid": v(-1206.25, 1303.34) * mm, "end": v(-1226.08, 1309.01) * mm});
            skArc(sketch, "E215", {"start": v(-1302.28, 1308.04) * mm, "mid": v(-1323.48, 1302.68) * mm, "end": v(-1302.28, 1297.32) * mm});
            skLineSegment(sketch, "E216", {"start": v(-1302.28, 1309.01) * mm, "end": v(-1302.28, 1308.04) * mm});
            skLineSegment(sketch, "E217", {"start": v(-1226.08, 1297.67) * mm, "end": v(-1226.08, 1297.32) * mm});
            skFitSpline(sketch, "E218.MirrorCS", {"points": [v(-1600.32, 430.53) * mm, v(-1723.02, 622.92) * mm, v(-1908.86, 774.94) * mm], "startDerivative": vector(-596.34, 198.24) * mm, "endDerivative": vector(-875.38, 6.78) * mm});
            skPoint(sketch, "E219", {"position": v(-1643.46, 545.72) * mm});
            skLineSegment(sketch, "E220.MirrorCS", {"start": v(-1475.82, 887.73) * mm, "end": v(-1475.82, 886.97) * mm});
            skPoint(sketch, "E221.orphan", {"position": v(-1615.52, 1064.77) * mm});
            skLineSegment(sketch, "E222", {"start": v(-1814.82, 968.51) * mm, "end": v(-1814.82, 805.43) * mm});
            skCircle(sketch, "E223", {"center": v(-1846.18, 886.97) * mm, "radius": 6.35 * mm});
            skCircle(sketch, "E224", {"center": v(-1698.5, 770.94) * mm, "radius": 38.1 * mm});
            skPoint(sketch, "E225.positionSnap0", {"position": v(-1920.46, 452.1) * mm});
            skPoint(sketch, "E226.MirrorP", {"position": v(-1643.46, 1228.22) * mm});
            skPoint(sketch, "E227.MirrorP", {"position": v(-1643.46, 1241.8) * mm});
            skPoint(sketch, "E228.MirrorP", {"position": v(-1643.46, 1214.63) * mm});
            skLineSegment(sketch, "E229", {"start": v(-1814.82, 805.43) * mm, "end": v(-1706.33, 886.97) * mm});
            skLineSegment(sketch, "E230.MirrorCS", {"start": v(-1814.82, 968.51) * mm, "end": v(-1706.33, 886.97) * mm});
            skCircle(sketch, "E231.MirrorC", {"center": v(-1826.7, 712.32) * mm, "radius": 38.1 * mm});
            skCircle(sketch, "E232.MirrorC", {"center": v(-1948.22, 519.1) * mm, "radius": 12.7 * mm});
            skPoint(sketch, "E233.MirrorP", {"position": v(-1924.36, 519.1) * mm});
            skFitSpline(sketch, "E234.MirrorCS", {"points": [v(-1920.46, 438.15) * mm, v(-1877.66, 622.66) * mm], "startDerivative": vector(168, 45.32) * mm, "endDerivative": vector(42.54, 297.2) * mm});
            skFitSpline(sketch, "E235.MirrorCS", {"points": [v(-1920.46, 438.15) * mm, v(-2007.42, 775.29) * mm], "startDerivative": vector(-410.48, -21.33) * mm, "endDerivative": vector(48.12, 416.26) * mm});
            skFitSpline(sketch, "E236", {"points": [v(-1724.26, 629.02) * mm, v(-1877.66, 622.66) * mm], "startDerivative": vector(-0.87, 82.52) * mm, "endDerivative": vector(-81, -110.74) * mm});
            skFitSpline(sketch, "E237", {"points": [v(-1876.89, 758.78) * mm, v(-2022.53, 621.87) * mm], "startDerivative": vector(-229.66, -105.01) * mm, "endDerivative": vector(-27.76, -191.38) * mm});
            skFitSpline(sketch, "E238.MirrorCS", {"points": [v(-1600.32, 1344.93) * mm, v(-1723.02, 1152.54) * mm, v(-1908.86, 1000.53) * mm], "startDerivative": vector(-596.34, -198.24) * mm, "endDerivative": vector(-875.38, -6.78) * mm});
            skLineSegment(sketch, "E239.MirrorCS", {"start": v(-1643.46, 1224.8) * mm, "end": v(-1643.46, 1231.65) * mm});
            skArc(sketch, "E240.MirrorCS", {"start": v(-1399.62, 1241.8) * mm, "mid": v(-1392.44, 1238.83) * mm, "end": v(-1389.46, 1231.65) * mm});
            skLineSegment(sketch, "E241.MirrorCS", {"start": v(-1389.46, 1231.65) * mm, "end": v(-1389.46, 1224.8) * mm});
            skArc(sketch, "E242.MirrorCS", {"start": v(-1643.46, 1231.65) * mm, "mid": v(-1640.49, 1238.83) * mm, "end": v(-1633.3, 1241.8) * mm});
            skCircle(sketch, "E243.MirrorC", {"center": v(-1948.22, 1254.84) * mm, "radius": 12.7 * mm});
            skFitSpline(sketch, "E244.MirrorCS", {"points": [v(-1920.46, 1335.8) * mm, v(-2007.42, 998.65) * mm], "startDerivative": vector(-410.48, 21.33) * mm, "endDerivative": vector(48.12, -416.26) * mm});
            skFitSpline(sketch, "E245.MirrorCS", {"points": [v(-1876.89, 1015.16) * mm, v(-2022.53, 1152.07) * mm], "startDerivative": vector(-229.66, 105.01) * mm, "endDerivative": vector(-27.76, 191.38) * mm});
            skCircle(sketch, "E246.MirrorC", {"center": v(-1698.5, 1003) * mm, "radius": 38.1 * mm});
            skPoint(sketch, "E247.MirrorP", {"position": v(-1924.36, 1254.84) * mm});
            skFitSpline(sketch, "E248.MirrorCS", {"points": [v(-1724.26, 1144.92) * mm, v(-1877.66, 1151.28) * mm], "startDerivative": vector(-0.87, -82.52) * mm, "endDerivative": vector(-81, 110.74) * mm});
            skLineSegment(sketch, "E249.MirrorCS", {"start": v(-1633.3, 1241.8) * mm, "end": v(-1399.62, 1241.8) * mm});
            skCircle(sketch, "E250.MirrorC", {"center": v(-1826.7, 1061.62) * mm, "radius": 38.1 * mm});
            skPoint(sketch, "E251.MirrorP", {"position": v(-1389.46, 1214.63) * mm});
            skPoint(sketch, "E252.MirrorP", {"position": v(-1920.46, 1321.84) * mm});
            skFitSpline(sketch, "E253.MirrorCS", {"points": [v(-1920.46, 1335.8) * mm, v(-1877.66, 1151.28) * mm], "startDerivative": vector(168, -45.32) * mm, "endDerivative": vector(42.54, -297.2) * mm});
            skPoint(sketch, "E254.MirrorP", {"position": v(-1389.46, 1241.8) * mm});
            skPoint(sketch, "E255.MirrorP", {"position": v(-1600.32, 1343.4) * mm});
            skLineSegment(sketch, "E256", {"start": v(-1876.89, 758.78) * mm, "end": v(-1876.89, 1015.16) * mm});
            skFitSpline(sketch, "E257", {"points": [v(-1724.26, 1144.92) * mm, v(-1724.26, 1146.45) * mm], "startDerivative": vector(0.09, 0.95) * mm, "endDerivative": vector(0.33, 1.62) * mm});
            skLineSegment(sketch, "E258.bottom", {"start": v(-1087.58, 487.68) * mm, "end": v(-1036.78, 487.68) * mm});
            skLineSegment(sketch, "E258.top", {"start": v(-1087.58, 468.63) * mm, "end": v(-1036.78, 468.63) * mm});
            skLineSegment(sketch, "E258.left", {"start": v(-1087.58, 487.68) * mm, "end": v(-1087.58, 468.63) * mm});
            skLineSegment(sketch, "E258.right", {"start": v(-1036.78, 487.68) * mm, "end": v(-1036.78, 468.63) * mm});
            skLineSegment(sketch, "E259.MirrorCS", {"start": v(-1087.58, 1306.83) * mm, "end": v(-1036.78, 1306.83) * mm});
            skLineSegment(sketch, "E260.MirrorCS", {"start": v(-1036.78, 1287.78) * mm, "end": v(-1036.78, 1306.83) * mm});
            skLineSegment(sketch, "E261.MirrorCS", {"start": v(-1087.58, 1287.78) * mm, "end": v(-1087.58, 1306.83) * mm});
            skLineSegment(sketch, "E262.MirrorCS", {"start": v(-1087.58, 1287.78) * mm, "end": v(-1036.78, 1287.78) * mm});
            skLineSegment(sketch, "E263.MirrorCS", {"start": v(-1594.67, 1015.93) * mm, "end": v(-1510.06, 1015.93) * mm});
            skLineSegment(sketch, "E264.MirrorCS", {"start": v(-1594.67, 1034.98) * mm, "end": v(-1594.67, 1015.93) * mm});
            skLineSegment(sketch, "E265.MirrorCS", {"start": v(-1510.06, 1034.98) * mm, "end": v(-1510.06, 1015.93) * mm});
            skLineSegment(sketch, "E266.MirrorCS", {"start": v(-1594.67, 1034.98) * mm, "end": v(-1510.06, 1034.98) * mm});
            skLineSegment(sketch, "E267.MirrorCS", {"start": v(-1594.67, 759.54) * mm, "end": v(-1510.06, 759.54) * mm});
            skLineSegment(sketch, "E268.MirrorCS", {"start": v(-1594.67, 740.49) * mm, "end": v(-1510.06, 740.49) * mm});
            skLineSegment(sketch, "E269.MirrorCS", {"start": v(-1594.67, 740.49) * mm, "end": v(-1594.67, 759.54) * mm});
            skLineSegment(sketch, "E270.MirrorCS", {"start": v(-1510.06, 740.49) * mm, "end": v(-1510.06, 759.54) * mm});
            skLineSegment(sketch, "E271.bottom", {"start": v(-1963.2, 1138.98) * mm, "end": v(-1905.61, 1138.98) * mm});
            skLineSegment(sketch, "E271.top", {"start": v(-1963.2, 1119.93) * mm, "end": v(-1905.61, 1119.93) * mm});
            skLineSegment(sketch, "E271.left", {"start": v(-1963.2, 1138.98) * mm, "end": v(-1963.2, 1119.93) * mm});
            skLineSegment(sketch, "E271.right", {"start": v(-1905.61, 1138.98) * mm, "end": v(-1905.61, 1119.93) * mm});
            skLineSegment(sketch, "E272", {"start": v(-1706.33, 886.97) * mm, "end": v(-2145.98, 886.97) * mm});
            skLineSegment(sketch, "E273.MirrorCS", {"start": v(-1963.2, 634.96) * mm, "end": v(-1905.61, 634.96) * mm});
            skLineSegment(sketch, "E274.MirrorCS", {"start": v(-1963.2, 654) * mm, "end": v(-1905.61, 654) * mm});
            skLineSegment(sketch, "E275.MirrorCS", {"start": v(-1963.2, 634.96) * mm, "end": v(-1963.2, 654) * mm});
            skLineSegment(sketch, "E276.MirrorCS", {"start": v(-1905.61, 634.96) * mm, "end": v(-1905.61, 654) * mm});
            skLineSegment(sketch, "E277", {"start": v(-2022.53, 1152.07) * mm, "end": v(-1877.66, 1151.28) * mm, "construction": true});
            skFitSpline(sketch, "E278.MirrorCS", {"points": [v(822.6, 1059.04) * mm, v(699.89, 1251.43) * mm, v(514.05, 1403.44) * mm], "startDerivative": vector(-596.34, 198.24) * mm, "endDerivative": vector(-875.38, 6.78) * mm});
            skLineSegment(sketch, "E279", {"start": v(608.09, 1597.02) * mm, "end": v(608.09, 1433.93) * mm});
            skCircle(sketch, "E280", {"center": v(576.73, 1515.47) * mm, "radius": 6.35 * mm});
            skCircle(sketch, "E281", {"center": v(724.4, 1399.44) * mm, "radius": 38.1 * mm});
            skPoint(sketch, "E282.positionSnap0", {"position": v(502.44, 1080.6) * mm});
            skLineSegment(sketch, "E283", {"start": v(608.09, 1433.93) * mm, "end": v(716.58, 1515.47) * mm});
            skLineSegment(sketch, "E284.MirrorCS", {"start": v(608.09, 1597.02) * mm, "end": v(716.58, 1515.47) * mm});
            skCircle(sketch, "E285.MirrorC", {"center": v(596.2, 1340.82) * mm, "radius": 38.1 * mm});
            skCircle(sketch, "E286.MirrorC", {"center": v(474.69, 1147.6) * mm, "radius": 12.7 * mm});
            skPoint(sketch, "E287.MirrorP", {"position": v(498.55, 1147.6) * mm});
            skFitSpline(sketch, "E288.MirrorCS", {"points": [v(502.44, 1066.65) * mm, v(545.24, 1252.65) * mm], "startDerivative": vector(168, 45.32) * mm, "endDerivative": vector(42.54, 297.2) * mm});
            skFitSpline(sketch, "E289.MirrorCS", {"points": [v(502.44, 1066.65) * mm, v(415.5, 1403.8) * mm], "startDerivative": vector(-410.48, -21.33) * mm, "endDerivative": vector(48.12, 416.26) * mm});
            skFitSpline(sketch, "E290", {"points": [v(698.65, 1257.52) * mm, v(545.24, 1252.65) * mm], "startDerivative": vector(-0.87, 82.52) * mm, "endDerivative": vector(-81, -110.74) * mm});
            skFitSpline(sketch, "E291", {"points": [v(546.02, 1387.28) * mm, v(400.38, 1250.38) * mm], "startDerivative": vector(-229.66, -105.01) * mm, "endDerivative": vector(-27.76, -191.38) * mm});
            skFitSpline(sketch, "E292.MirrorCS", {"points": [v(822.6, 1973.44) * mm, v(699.89, 1781.05) * mm, v(514.05, 1629.03) * mm], "startDerivative": vector(-596.34, -198.24) * mm, "endDerivative": vector(-875.38, -6.78) * mm});
            skCircle(sketch, "E293.MirrorC", {"center": v(474.69, 1883.34) * mm, "radius": 12.7 * mm});
            skFitSpline(sketch, "E294.MirrorCS", {"points": [v(502.44, 1964.3) * mm, v(415.5, 1627.16) * mm], "startDerivative": vector(-410.48, 21.33) * mm, "endDerivative": vector(48.12, -416.26) * mm});
            skFitSpline(sketch, "E295.MirrorCS", {"points": [v(546.02, 1643.67) * mm, v(400.38, 1780.57) * mm], "startDerivative": vector(-229.66, 105.01) * mm, "endDerivative": vector(-27.76, 191.38) * mm});
            skCircle(sketch, "E296.MirrorC", {"center": v(724.4, 1631.5) * mm, "radius": 38.1 * mm});
            skPoint(sketch, "E297.MirrorP", {"position": v(498.55, 1883.34) * mm});
            skFitSpline(sketch, "E298.MirrorCS", {"points": [v(698.65, 1773.43) * mm, v(545.25, 1779.78) * mm], "startDerivative": vector(-0.87, -82.52) * mm, "endDerivative": vector(-81, 110.74) * mm});
            skCircle(sketch, "E299.MirrorC", {"center": v(596.2, 1690.13) * mm, "radius": 38.1 * mm});
            skPoint(sketch, "E300.MirrorP", {"position": v(502.44, 1950.35) * mm});
            skFitSpline(sketch, "E301.MirrorCS", {"points": [v(502.44, 1964.3) * mm, v(545.25, 1779.78) * mm], "startDerivative": vector(168, -45.32) * mm, "endDerivative": vector(42.54, -297.2) * mm});
            skLineSegment(sketch, "E302", {"start": v(546.02, 1387.28) * mm, "end": v(546.02, 1643.67) * mm});
            skFitSpline(sketch, "E303", {"points": [v(698.65, 1773.43) * mm, v(698.65, 1774.95) * mm], "startDerivative": vector(0.09, 0.95) * mm, "endDerivative": vector(0.33, 1.62) * mm});
            skFitSpline(sketch, "E304", {"points": [v(822.6, 1973.44) * mm, v(822.6, 1059.04) * mm], "startDerivative": vector(461.05, -112.6) * mm, "endDerivative": vector(-642.98, -332.06) * mm});
            skLineSegment(sketch, "E305.bottom", {"start": v(828.24, 1644.43) * mm, "end": v(912.85, 1644.43) * mm});
            skLineSegment(sketch, "E305.top", {"start": v(828.24, 1663.48) * mm, "end": v(912.85, 1663.48) * mm});
            skLineSegment(sketch, "E305.left", {"start": v(828.24, 1644.43) * mm, "end": v(828.24, 1663.48) * mm});
            skLineSegment(sketch, "E305.right", {"start": v(912.85, 1644.43) * mm, "end": v(912.85, 1663.48) * mm});
            skLineSegment(sketch, "E306", {"start": v(716.58, 1515.47) * mm, "end": v(1057.55, 1515.47) * mm});
            skLineSegment(sketch, "E307", {"start": v(917.78, 1187.81) * mm, "end": v(789.6, 1187.81) * mm});
            skLineSegment(sketch, "E308", {"start": v(779.45, 1177.65) * mm, "end": v(779.45, 1170.8) * mm});
            skLineSegment(sketch, "E309", {"start": v(789.6, 1160.64) * mm, "end": v(906.82, 1160.64) * mm});
            skPoint(sketch, "E310.visualSharp", {"position": v(779.45, 1187.81) * mm});
            skArc(sketch, "E310.filletArc", {"start": v(789.6, 1187.81) * mm, "mid": v(782.42, 1184.84) * mm, "end": v(779.45, 1177.65) * mm});
            skPoint(sketch, "E311.visualSharp", {"position": v(779.45, 1160.64) * mm});
            skArc(sketch, "E311.filletArc", {"start": v(779.45, 1170.8) * mm, "mid": v(782.42, 1163.61) * mm, "end": v(789.6, 1160.64) * mm});
            skFitSpline(sketch, "E312.MirrorCS", {"points": [v(822.6, 1059.04) * mm, v(699.89, 1251.43) * mm, v(514.05, 1403.44) * mm], "startDerivative": vector(-596.34, 198.24) * mm, "endDerivative": vector(-875.38, 6.78) * mm});
            skPoint(sketch, "E313", {"position": v(779.45, 1174.23) * mm});
            skArc(sketch, "E314.MirrorCS", {"start": v(789.6, 1843.13) * mm, "mid": v(782.42, 1846.1) * mm, "end": v(779.45, 1853.3) * mm});
            skArc(sketch, "E315.MirrorCS", {"start": v(779.45, 1860.15) * mm, "mid": v(782.42, 1867.34) * mm, "end": v(789.6, 1870.31) * mm});
            skLineSegment(sketch, "E316.MirrorCS", {"start": v(779.45, 1853.3) * mm, "end": v(779.45, 1860.15) * mm});
            skLineSegment(sketch, "E317.MirrorCS", {"start": v(913.52, 1843.13) * mm, "end": v(789.6, 1843.13) * mm});
            skPoint(sketch, "E318.MirrorP", {"position": v(779.45, 1870.31) * mm});
            skPoint(sketch, "E319.MirrorP", {"position": v(779.45, 1843.13) * mm});
            skPoint(sketch, "E320.MirrorP", {"position": v(779.45, 1856.72) * mm});
            skLineSegment(sketch, "E321.MirrorCS", {"start": v(789.6, 1870.31) * mm, "end": v(903.85, 1870.31) * mm});
            skFitSpline(sketch, "E322.trimOffspring", {"points": [v(822.6, 1973.44) * mm, v(822.6, 1059.04) * mm], "startDerivative": vector(461.05, -112.6) * mm, "endDerivative": vector(-642.98, -332.06) * mm});
            skLineSegment(sketch, "E323.MirrorCS", {"start": v(828.24, 1367.47) * mm, "end": v(912.85, 1367.47) * mm});
            skLineSegment(sketch, "E324.MirrorCS", {"start": v(828.24, 1386.52) * mm, "end": v(912.85, 1386.52) * mm});
            skLineSegment(sketch, "E325.MirrorCS", {"start": v(828.24, 1386.52) * mm, "end": v(828.24, 1367.47) * mm});
            skLineSegment(sketch, "E326.MirrorCS", {"start": v(912.85, 1386.52) * mm, "end": v(912.85, 1367.47) * mm});
            skLineSegment(sketch, "E327", {"start": v(545.24, 1252.65) * mm, "end": v(400.38, 1250.38) * mm, "construction": true});
            skLineSegment(sketch, "E328.bottom", {"start": v(515.72, 1279.54) * mm, "end": v(458.12, 1279.54) * mm});
            skLineSegment(sketch, "E328.top", {"start": v(515.72, 1260.49) * mm, "end": v(458.12, 1260.49) * mm});
            skLineSegment(sketch, "E328.left", {"start": v(515.72, 1279.54) * mm, "end": v(515.72, 1260.49) * mm});
            skLineSegment(sketch, "E328.right", {"start": v(458.12, 1279.54) * mm, "end": v(458.12, 1260.49) * mm});
            skLineSegment(sketch, "E329.MirrorCS", {"start": v(515.72, 1751.4) * mm, "end": v(458.12, 1751.4) * mm});
            skLineSegment(sketch, "E330.MirrorCS", {"start": v(515.72, 1770.46) * mm, "end": v(458.12, 1770.46) * mm});
            skLineSegment(sketch, "E331.MirrorCS", {"start": v(458.12, 1751.4) * mm, "end": v(458.12, 1770.46) * mm});
            skLineSegment(sketch, "E332.MirrorCS", {"start": v(515.72, 1751.4) * mm, "end": v(515.72, 1770.46) * mm});
            skSolve(sketch);
        }
        {
            var Q0;
            Q0 = qSketchRegion(id + "F8", true);
            extrude(context, id + "F9", {"entities" : qUnion([Q0]), "depth" : 25.4 * mm, "offsetDistance" : 25.4 * mm});
        }
    });
